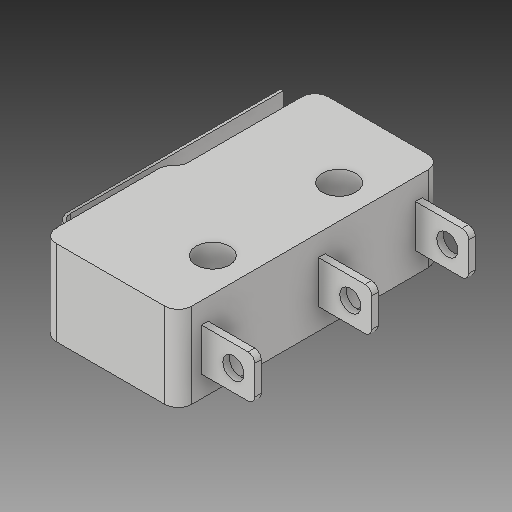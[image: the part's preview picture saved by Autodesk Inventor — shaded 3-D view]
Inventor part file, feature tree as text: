
AUTODESK INVENTOR PART (.ipt)
format: ipt  version: 2019 (Build 230136000, 136)  size: 218,624 bytes
history: native  units: mm
features: extrude x4, sketch x4, fillet x2
ambient origin geometry x8: Origin, YZ Plane, XZ Plane, XY Plane, X Axis, Y Axis, Z Axis, Center Point
bodies: Solid1 (feature_tree)
feature tree (10):
  extrude  "Extrusion1"  Depth=19.8mm
  extrude  "Extrusion2"  Depth=2.5mm
  extrude  "Extrusion3"  TaperAngle=0.0deg  [1 undecoded]
  extrude  "Extrusion4"  Depth=9.5mm
  fillet  "Fillet1"  [1 undecoded]
  fillet  "Fillet2"  Radius=2.5mm
  sketch  "Sketch1"  dims[d0=10.2mm d1=19.8mm]
  sketch  "Sketch2"  dims[d3=90.0deg d4=2.5mm]
  sketch  "Sketch3"  dims[d5=5.1mm d6=0.0mm]
  sketch  "Sketch4"  dims[d7=2.5mm d8=9.5mm d9=90.0deg d10=2.5mm d11=9.5mm d12=0.0mm d13=135.0deg d14=3.075914mm d15=6.4mm d16=0.0mm d17=2.8mm d18=90.0deg d19=1.9mm d20=0.0mm d21=2.0mm d22=2.0mm d23=0.2mm d24=90.0deg d25=0.2mm d26=3.8mm d27=0.0mm d28=2.0mm d29=8.8mm d30=7.3mm d31=8.0mm d32=0.5mm d33=8.0mm d34=0.5mm d35=8.0mm d36=0.5mm d37=3.2mm d38=0.0mm d39=3.2mm d40=1.6mm d41=40.0mm d42=0.0mm d43=1.0mm d44=0.5mm]
note: 2 required parameter values undecoded (feature->parameter linkage not recoverable at this tier; creation-order binding heuristic only, values carry confidence <= 0.55)
